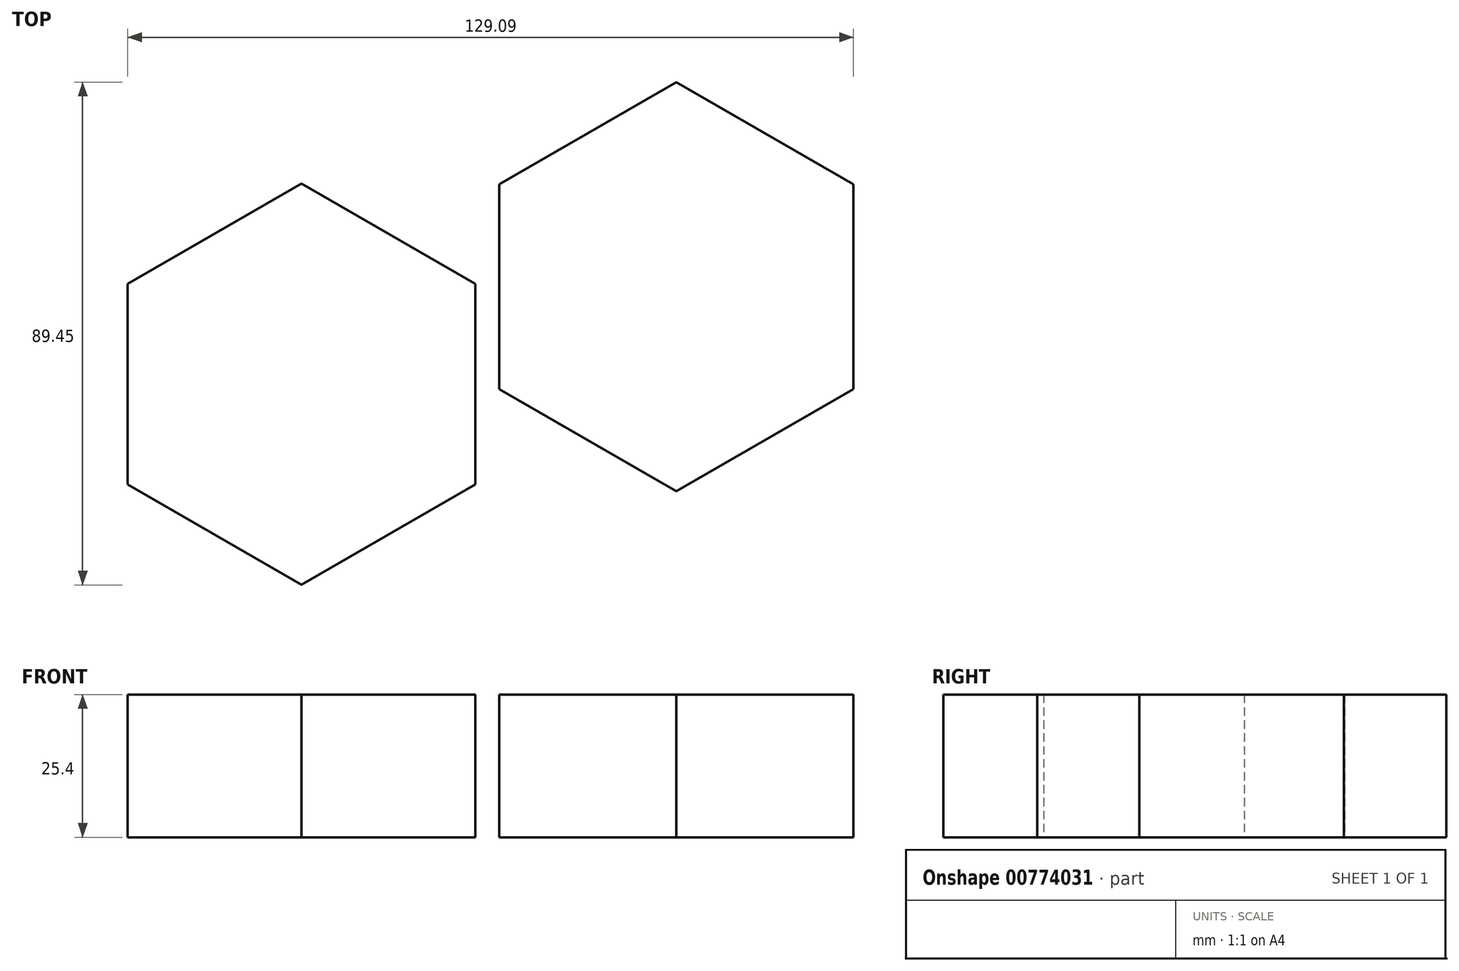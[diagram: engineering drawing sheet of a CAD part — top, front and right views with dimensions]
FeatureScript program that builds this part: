
annotation { "Feature Type Name" : "Feature", "Feature Type Description" : "" }
export const myFeature = defineFeature(function(context is Context, id is Id, definition is map)
    precondition{}
    {
        {
            var Q0;
            Q0=qCreatedBy(makeId("Top.planeOp"),FACE);
            var sketch = newSketch(context, id + "F0", { "sketchPlane" : qUnion([Q0])});
            skCircle(sketch, "E0.cCircle", {"center": v(-69.88, 17.43) * mm, "radius": 30.9 * mm, "construction": true});
            skLineSegment(sketch, "E0.0", {"start": v(-38.97, 35.28) * mm, "end": v(-38.97, -0.41) * mm});
            skLineSegment(sketch, "E0.1", {"start": v(-38.97, -0.41) * mm, "end": v(-69.88, -18.26) * mm});
            skLineSegment(sketch, "E0.2", {"start": v(-69.88, -18.26) * mm, "end": v(-100.78, -0.41) * mm});
            skLineSegment(sketch, "E0.3", {"start": v(-100.78, -0.41) * mm, "end": v(-100.78, 35.28) * mm});
            skLineSegment(sketch, "E0.4", {"start": v(-100.78, 35.28) * mm, "end": v(-69.88, 53.12) * mm});
            skLineSegment(sketch, "E0.5", {"start": v(-69.88, 53.12) * mm, "end": v(-38.97, 35.28) * mm});
            skPoint(sketch, "E0.0.midPoint", {"position": v(-38.97, 17.43) * mm});
            skCircle(sketch, "E1.cCircle", {"center": v(-3.22, 34.8) * mm, "radius": 31.52 * mm, "construction": true});
            skLineSegment(sketch, "E1.0", {"start": v(28.3, 53) * mm, "end": v(28.3, 16.6) * mm});
            skLineSegment(sketch, "E1.1", {"start": v(28.3, 16.6) * mm, "end": v(-3.22, -1.6) * mm});
            skLineSegment(sketch, "E1.2", {"start": v(-3.22, -1.6) * mm, "end": v(-34.74, 16.6) * mm});
            skLineSegment(sketch, "E1.3", {"start": v(-34.74, 16.6) * mm, "end": v(-34.74, 53) * mm});
            skLineSegment(sketch, "E1.4", {"start": v(-34.74, 53) * mm, "end": v(-3.22, 71.19) * mm});
            skLineSegment(sketch, "E1.5", {"start": v(-3.22, 71.19) * mm, "end": v(28.3, 53) * mm});
            skPoint(sketch, "E1.0.midPoint", {"position": v(28.3, 34.8) * mm});
            skSolve(sketch);
        }
        {
            var Q0;
            Q0=makeQuery(id+"F0.imprint","IMPRINT",FACE,{"disambiguationData":[TD([[makeQuery(id+"F0.imprint","IMPRINT",EDGE,{"derivedFrom":sQuery(id+"F0.wireOp",EDGE,"E0.0")}),-1.0]])]});
            var Q1;
            Q1=makeQuery(id+"F0.imprint","IMPRINT",FACE,{"disambiguationData":[TD([[makeQuery(id+"F0.imprint","IMPRINT",EDGE,{"derivedFrom":sQuery(id+"F0.wireOp",EDGE,"E1.0")}),-1.0]])]});
            extrude(context, id + "F1", {"entities" : qUnion([Q0, Q1]), "depth" : 25.4 * mm, "offsetDistance" : 25.4 * mm});
        }
    });
